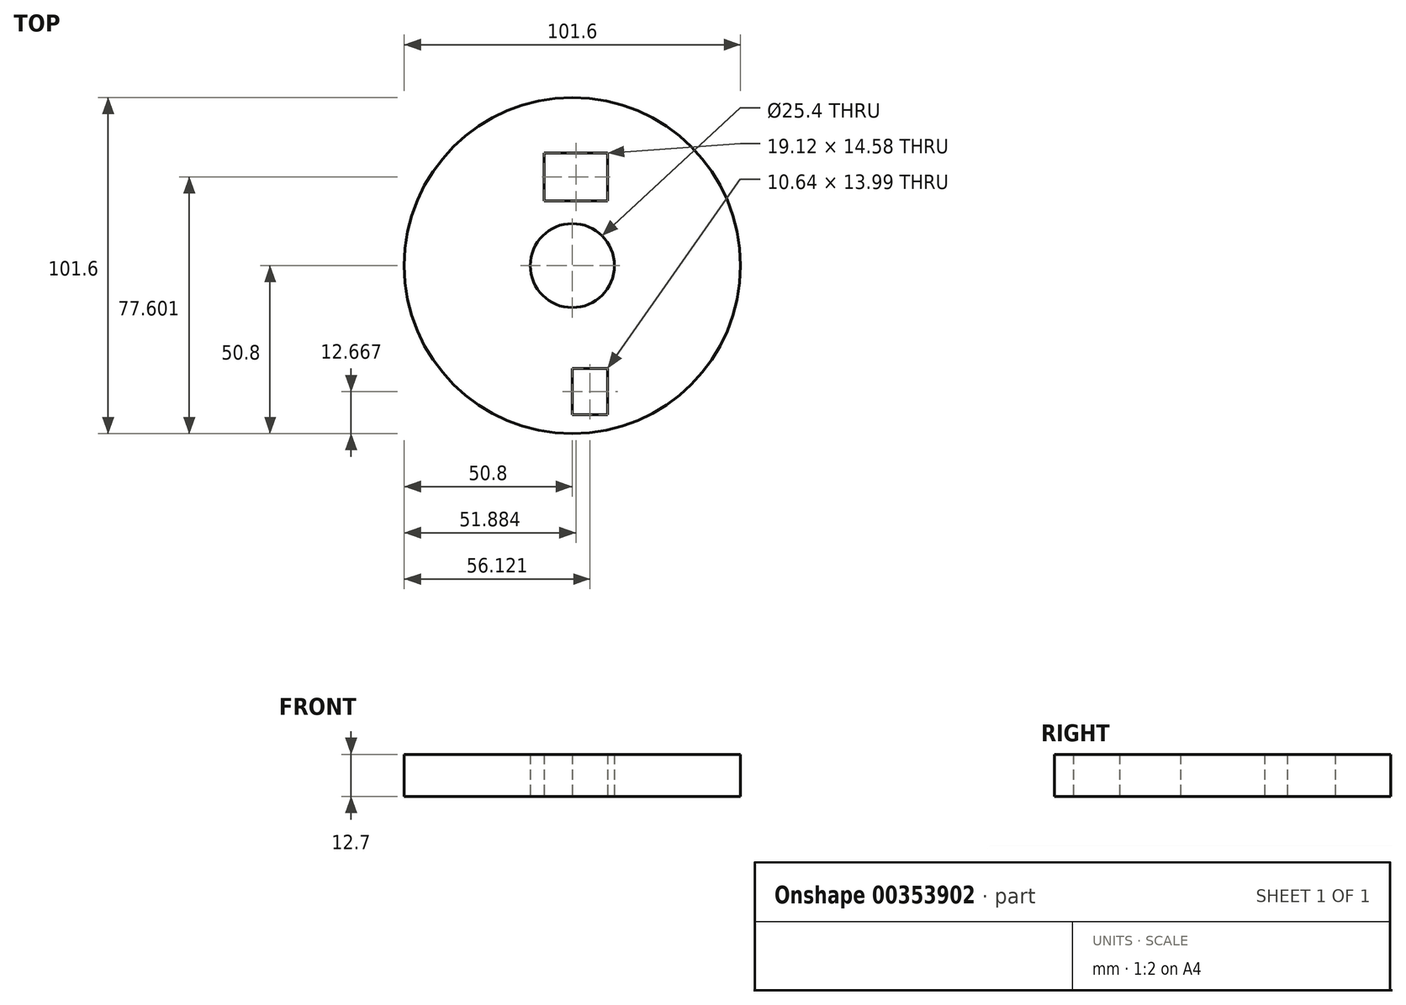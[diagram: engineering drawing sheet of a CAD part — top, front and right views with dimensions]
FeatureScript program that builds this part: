
annotation { "Feature Type Name" : "Feature", "Feature Type Description" : "" }
export const myFeature = defineFeature(function(context is Context, id is Id, definition is map)
    precondition{}
    {
        {
            var Q0;
            Q0=qCreatedBy(makeId("Top.planeOp"),FACE);
            var sketch = newSketch(context, id + "F0", { "sketchPlane" : qUnion([Q0])});
            skCircle(sketch, "E0", {"center": v(0, 0) * mm, "radius": 50.8 * mm});
            skCircle(sketch, "E1", {"center": v(0, 0) * mm, "radius": 12.7 * mm});
            skLineSegment(sketch, "E2.bottom", {"start": v(-8.47, 34.1) * mm, "end": v(10.64, 34.1) * mm});
            skLineSegment(sketch, "E2.top", {"start": v(-8.47, 19.5) * mm, "end": v(10.64, 19.5) * mm});
            skLineSegment(sketch, "E2.left", {"start": v(-8.47, 34.1) * mm, "end": v(-8.47, 19.5) * mm});
            skLineSegment(sketch, "E2.right", {"start": v(10.64, 34.1) * mm, "end": v(10.64, 19.5) * mm});
            skLineSegment(sketch, "E3.bottom", {"start": v(0, -31.14) * mm, "end": v(10.64, -31.14) * mm});
            skLineSegment(sketch, "E3.top", {"start": v(0, -45.13) * mm, "end": v(10.64, -45.13) * mm});
            skLineSegment(sketch, "E3.left", {"start": v(0, -31.14) * mm, "end": v(0, -45.13) * mm});
            skLineSegment(sketch, "E3.right", {"start": v(10.64, -31.14) * mm, "end": v(10.64, -45.13) * mm});
            skSolve(sketch);
        }
        {
            var Q0;
            Q0 = qSketchRegion(id + "F0", true);
            extrude(context, id + "F1", {"entities" : qUnion([Q0]), "depth" : 12.7 * mm});
        }
    });
